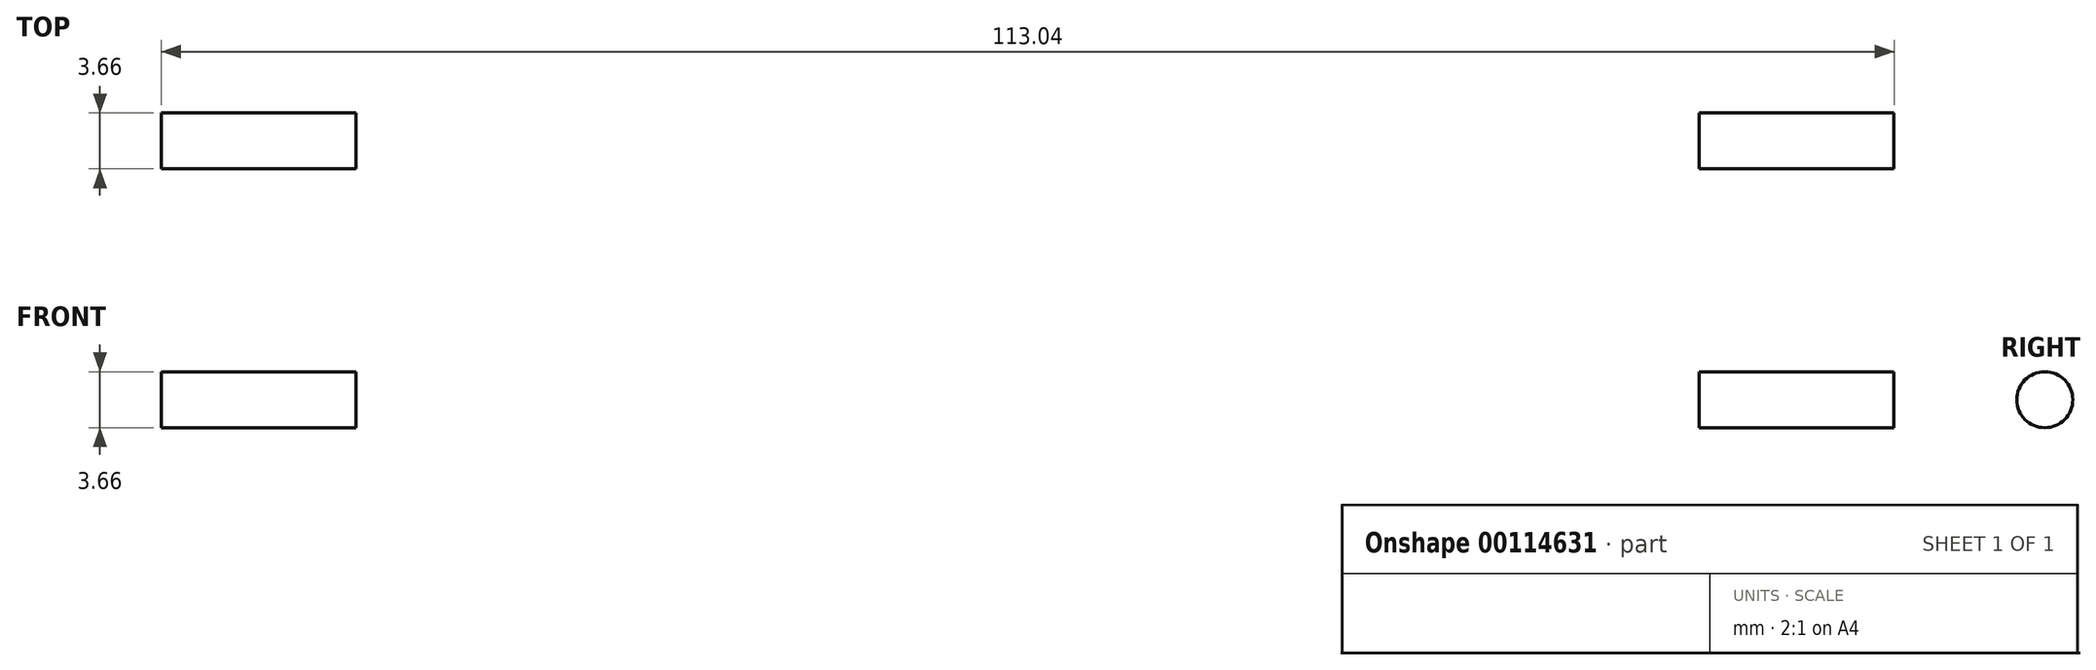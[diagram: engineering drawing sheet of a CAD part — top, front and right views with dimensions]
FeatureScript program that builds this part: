
annotation { "Feature Type Name" : "Feature", "Feature Type Description" : "" }
export const myFeature = defineFeature(function(context is Context, id is Id, definition is map)
    precondition{}
    {
        {
            var Q0;
            Q0=qCreatedBy(makeId("Top.planeOp"),FACE);
            var sketch = newSketch(context, id + "F0", { "sketchPlane" : qUnion([Q0])});
            skLineSegment(sketch, "E0.bottom", {"start": v(56.52, -12.7) * mm, "end": v(-56.52, -12.7) * mm});
            skLineSegment(sketch, "E0.top", {"start": v(56.52, 12.7) * mm, "end": v(-56.52, 12.7) * mm});
            skLineSegment(sketch, "E0.left", {"start": v(56.52, -12.7) * mm, "end": v(56.52, 12.7) * mm});
            skLineSegment(sketch, "E0.right", {"start": v(-56.52, -12.7) * mm, "end": v(-56.52, 12.7) * mm});
            skPoint(sketch, "E0.middle", {"position": v(0, 0) * mm});
            skSolve(sketch);
        }
        {
            var Q0;
            Q0 = qSketchRegion(id + "F0", true);
            extrude(context, id + "F1", {"entities" : qUnion([Q0]), "depth" : 6.35 * mm});
        }
        {
            var Q0;
            Q0=makeQuery(id+"F1.opExtrude","CAP_FACE",FACE,{"disambiguationData":[OSD([sQuery(id+"F0.wireOp",EDGE,"E0.bottom"),sQuery(id+"F0.wireOp",EDGE,"E0.top"),sQuery(id+"F0.wireOp",EDGE,"E0.left"),sQuery(id+"F0.wireOp",EDGE,"E0.right")])],"isStart":false});
            var sketch = newSketch(context, id + "F2", { "sketchPlane" : qUnion([Q0])});
            skCircle(sketch, "E1", {"center": v(0, 0) * mm, "radius": 3.81 * mm});
            skSolve(sketch);
        }
        {
            var Q0;
            Q0 = qSketchRegion(id + "F2", true);
            extrude(context, id + "F3", {"entities" : qUnion([Q0]), "operationType" : NewBodyOperationType.REMOVE, "endBound" : BoundingType.THROUGH_ALL, "oppositeDirection" : true, "depth" : 25.4 * mm});
        }
        {
            var Q0;
            Q0=makeQuery(id+"F1.opExtrude","CAP_FACE",FACE,{"disambiguationData":[OSD([sQuery(id+"F0.wireOp",EDGE,"E0.bottom"),sQuery(id+"F0.wireOp",EDGE,"E0.top"),sQuery(id+"F0.wireOp",EDGE,"E0.left"),sQuery(id+"F0.wireOp",EDGE,"E0.right")])],"isStart":true});
            var sketch = newSketch(context, id + "F4", { "sketchPlane" : qUnion([Q0])});
            skLineSegment(sketch, "E2", {"start": v(-43.82, -12.7) * mm, "end": v(-43.82, 12.7) * mm});
            skPoint(sketch, "E3", {"position": v(-56.52, 12.7) * mm});
            skPoint(sketch, "E4", {"position": v(-43.82, 12.7) * mm});
            skLineSegment(sketch, "E5", {"start": v(0, 0) * mm, "end": v(0, 12.7) * mm, "construction": true});
            skLineSegment(sketch, "E6.MirrorCS", {"start": v(43.82, -12.7) * mm, "end": v(43.82, 12.7) * mm});
            skSolve(sketch);
        }
        {
            var Q0;
            {var subQ0=sQuery(id+"F4.wireOp",EDGE,"E2");Q0=makeQuery(id+"F4.imprint","IMPRINT",FACE,{"disambiguationData":[TD([[makeQuery(id+"F4.imprint","IMPRINT",EDGE,{"derivedFrom":subQ0}),1.0]])]});}
            var Q1;
            {var subQ0=sQuery(id+"F4.wireOp",EDGE,"E6.MirrorCS");Q1=makeQuery(id+"F4.imprint","IMPRINT",FACE,{"disambiguationData":[TD([[makeQuery(id+"F4.imprint","IMPRINT",EDGE,{"derivedFrom":subQ0}),-1.0]])]});}
            extrude(context, id + "F5", {"entities" : qUnion([Q0, Q1]), "operationType" : NewBodyOperationType.ADD, "depth" : 12.7 * mm});
        }
        {
            var Q0;
            {var subQ0=sQuery(id+"F0.wireOp",EDGE,"E0.right");Q0=makeQuery(id+"F5.boolean.opBoolean","MERGE",FACE,{"derivedFrom":[makeQuery(id+"F1.opExtrude","SWEPT_FACE",FACE,{"disambiguationData":[OSD([subQ0])]}),makeQuery(id+"F5.opExtrude","SWEPT_FACE",FACE,{"disambiguationData":[OSD([subQ0])]})]});}
            var sketch = newSketch(context, id + "F6", { "sketchPlane" : qUnion([Q0])});
            skLineSegment(sketch, "E7", {"start": v(0, -12.7) * mm, "end": v(0, -6.35) * mm, "construction": true});
            skPoint(sketch, "E7.endSnap0", {"position": v(0, -12.7) * mm});
            skLineSegment(sketch, "E8", {"start": v(0, -6.35) * mm, "end": v(6.35, -6.35) * mm, "construction": true});
            skLineSegment(sketch, "E9.MirrorCS", {"start": v(0, -6.35) * mm, "end": v(-6.35, -6.35) * mm, "construction": true});
            skCircle(sketch, "E10", {"center": v(-6.35, -6.35) * mm, "radius": 1.83 * mm});
            skCircle(sketch, "E11.MirrorC", {"center": v(6.35, -6.35) * mm, "radius": 1.83 * mm});
            skSolve(sketch);
        }
        {
            var Q0;
            Q0=makeQuery(id+"F6.imprint","IMPRINT",FACE,{"disambiguationData":[TD([[makeQuery(id+"F6.imprint","IMPRINT",EDGE,{"derivedFrom":sQuery(id+"F6.wireOp",EDGE,"E10")}),1.0]])]});
            var Q1;
            Q1=makeQuery(id+"F6.imprint","IMPRINT",FACE,{"disambiguationData":[TD([[makeQuery(id+"F6.imprint","IMPRINT",EDGE,{"derivedFrom":sQuery(id+"F6.wireOp",EDGE,"E11.MirrorC")}),-1.0]])]});
            extrude(context, id + "F7", {"entities" : qUnion([Q0, Q1]), "operationType" : NewBodyOperationType.REMOVE, "oppositeDirection" : true, "depth" : 254 * mm});
        }
    });
